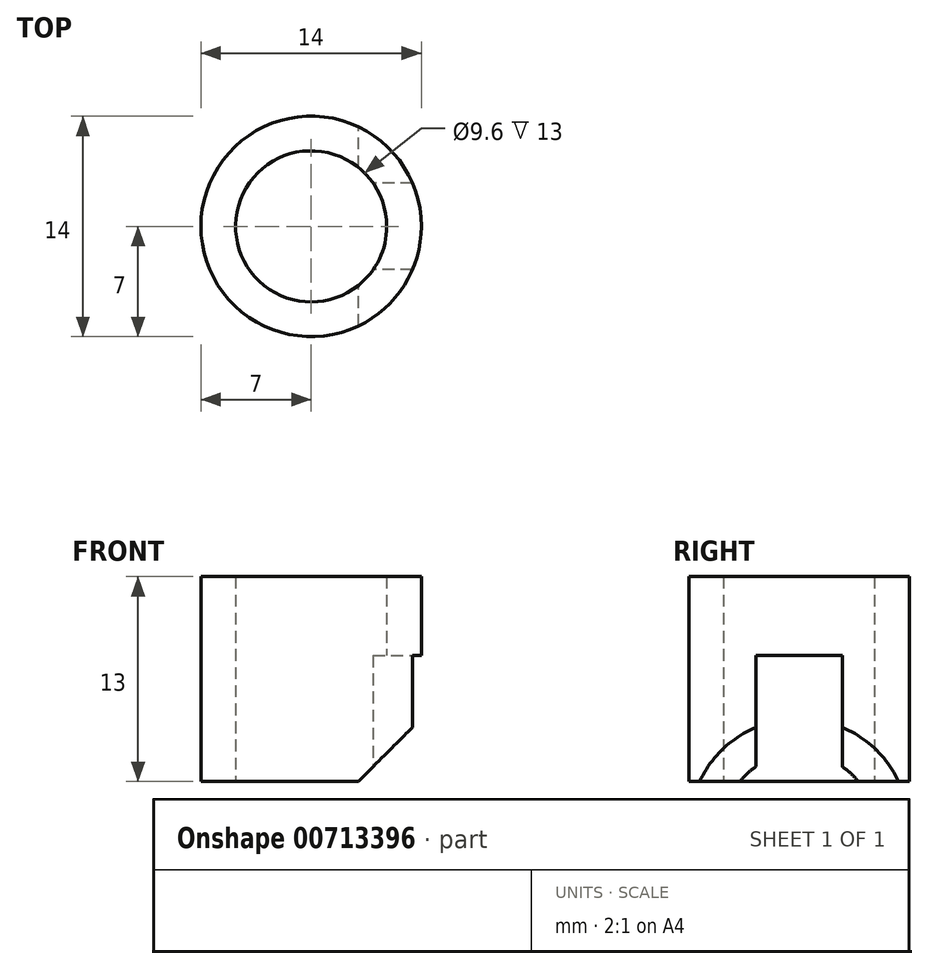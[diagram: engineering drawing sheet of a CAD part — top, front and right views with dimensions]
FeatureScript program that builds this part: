
annotation { "Feature Type Name" : "Feature", "Feature Type Description" : "" }
export const myFeature = defineFeature(function(context is Context, id is Id, definition is map)
    precondition{}
    {
        {
            var Q0;
            Q0=qCreatedBy(makeId("Top.planeOp"),FACE);
            var sketch = newSketch(context, id + "F0", { "sketchPlane" : qUnion([Q0])});
            skCircle(sketch, "E0", {"center": v(0, 0) * mm, "radius": 4.8 * mm});
            skCircle(sketch, "E1", {"center": v(0, 0) * mm, "radius": 7 * mm});
            skSolve(sketch);
        }
        {
            var Q0;
            Q0 = qSketchRegion(id + "F0", true);
            extrude(context, id + "F1", {"entities" : qUnion([Q0]), "depth" : 13 * mm, "offsetDistance" : 25 * mm});
        }
        {
            var Q0;
            Q0=qCreatedBy(makeId("Top.planeOp"),FACE);
            var sketch = newSketch(context, id + "F2", { "sketchPlane" : qUnion([Q0])});
            skLineSegment(sketch, "E2.bottom", {"start": v(3.2, 2.75) * mm, "end": v(10.03, 2.75) * mm});
            skLineSegment(sketch, "E2.top", {"start": v(3.2, -2.75) * mm, "end": v(10.03, -2.75) * mm});
            skLineSegment(sketch, "E2.left", {"start": v(3.2, 2.75) * mm, "end": v(3.2, -2.75) * mm});
            skLineSegment(sketch, "E2.right", {"start": v(10.03, 2.75) * mm, "end": v(10.03, -2.75) * mm});
            skSolve(sketch);
        }
        {
            var Q0;
            Q0 = qSketchRegion(id + "F2", true);
            extrude(context, id + "F3", {"entities" : qUnion([Q0]), "operationType" : NewBodyOperationType.REMOVE, "depth" : 8 * mm, "offsetDistance" : 25 * mm});
        }
        {
            var Q0;
            Q0=qCreatedBy(makeId("Front.planeOp"),FACE);
            var sketch = newSketch(context, id + "F4", { "sketchPlane" : qUnion([Q0])});
            skLineSegment(sketch, "E3", {"start": v(6.5, 0) * mm, "end": v(6.5, 3.5) * mm});
            skLineSegment(sketch, "E4", {"start": v(6.5, 3.5) * mm, "end": v(3, 0) * mm});
            skLineSegment(sketch, "E5", {"start": v(3, 0) * mm, "end": v(6.5, 0) * mm});
            skSolve(sketch);
        }
        {
            var Q0;
            Q0 = qSketchRegion(id + "F4", true);
            extrude(context, id + "F5", {"entities" : qUnion([Q0]), "operationType" : NewBodyOperationType.REMOVE, "endBound" : BoundingType.SYMMETRIC, "depth" : 25 * mm, "offsetDistance" : 25 * mm});
        }
    });
